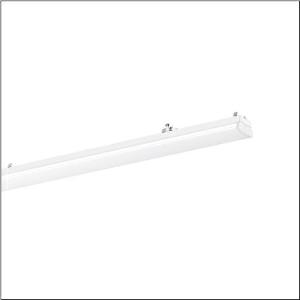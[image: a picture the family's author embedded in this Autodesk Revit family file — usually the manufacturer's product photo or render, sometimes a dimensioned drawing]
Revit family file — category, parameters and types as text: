
# Revit family: licross_r__11_recessed_opal_mo_51tl1ddn46xg_c64a
name_source: partatom
category: Lighting Fixtures
units: mm (PartAtom-declared; Revit-internal decimal feet)

## family parameters
Cut with Voids When Loaded = No
Host = Face
Light Source = No
Part Type = Normal
Room Calculation Point = No
Round Connector Dimension = Use Diameter
Shared = No

## types (1)
- --- (1 x LED, 6320 lm, 35.2 W, 4000K)
    Apparent Load = 35 VA
    CIE Flux Codes = 44 73 91 87 100
    Color Rendering = 80
    Color Temperature = 4000K
    Default Elevation = 1800 mm
    Description = Licross® 11 recessed opal MO, luminaire insert, of sheet steel, coil coated, white, length: 1.500mm, width: 76mm, height: 87mm, LED rated luminous flux: 6.320lm, light colour: 840, control gear: DALI 2, with plug, 5-pole, with phase selection, mains connection: 220..240V, AC, 50/60Hz, rated input power: 35W, halogen-free wiring, primary optical cover: cover, of PMMA, light emission: direct with ceiling illumination distribution, primary light characteristic: symmetric, protection rating (complete): IP40, insulation class (complete): insulation class I (protective earthing), certification: CE, ENEC, VDE, UKCA, protection symbol: D if used in an environment without relevant dust loads with corresponding accessories, impact resistance: IK06, permissible ambient temperature for indoor applications: -25..+40°C, corresponds to IFS (International Featured Standards) requirements for safety and quality in the food industry, reducing of maximum allowable ambient temperature of 5°C with ceiling mounting, LABS conformity tested according to VDMA 24364:2018-05, packaging unit: 1 piece
    Height = 83 mm
    Lamp = 1 x LED
    Lamp Light Flux = 6320 lm
    Lamp Power = 35.2 W
    Lamp count = 1
    Length = 1500 mm
    Luminous efficacy = 180 lm/W
    Manufacturer = Siteco
    ModVariant = No
    Model = 51TL1DDN46XG
    Mounting Place = Ceiling
    Mounting Type = Pendant
    Number of Poles = 1
    OnlyDefault = Yes
    Power Factor = 1
    Product Name = Licross® 11 recessed opal MO
    Product group = luminaire insert
    ProductGroupID = 901
    Protection Class = Protection class I
    Protection Degree = IP 40
    RLX_Detail_Level = 1
    RLX_Emergency_Light_Flux = 0 lm
    RLX_Emergency_Type = 0
    RLX_Emergency_Type_DB = No
    RlxData = <blob elided: 26677 chars, md5=cc12ce56>
    Socket = socket
    Standby Power = 0 W
    System Light Flux = 6320 lm
    System Power = 35 W
    Type Comments = factory setting: luminous flux: 100 % | dim-lin: 254 | 238 mA
    Type Image = l_1313666.jpg
    URL = http://relux.com
    VarID = @adj_045169
    Voltage = 0 V
    Weight = 0.00 kg
    Width = 76 mm

## geometry (parser evidence)
native form markers: Blend x4, Sweep x13
no freeform markers — native parametric forms only
